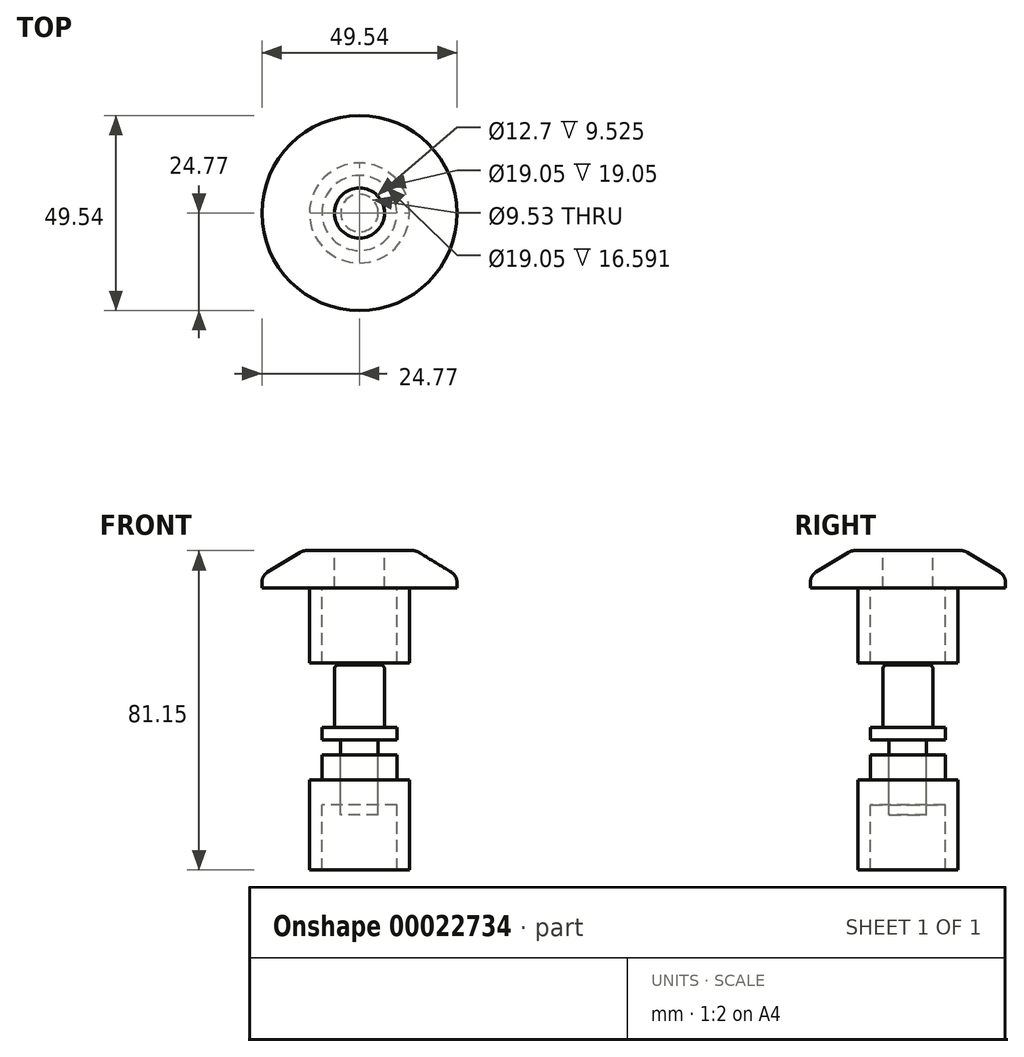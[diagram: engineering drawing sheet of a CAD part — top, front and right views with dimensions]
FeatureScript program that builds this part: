
annotation { "Feature Type Name" : "Feature", "Feature Type Description" : "" }
export const myFeature = defineFeature(function(context is Context, id is Id, definition is map)
    precondition{}
    {
        {
            var Q0;
            Q0=qCreatedBy(makeId("Front.planeOp"),FACE);
            var sketch = newSketch(context, id + "F0", { "sketchPlane" : qUnion([Q0])});
            skLineSegment(sketch, "E0", {"start": v(0, 45.49) * mm, "end": v(0, -47.52) * mm, "construction": true});
            skLineSegment(sketch, "E1", {"start": v(-6.35, 9.53) * mm, "end": v(-14.35, 9.53) * mm});
            skLineSegment(sketch, "E2", {"start": v(-14.35, 9.53) * mm, "end": v(-24.77, 3.17) * mm});
            skLineSegment(sketch, "E3", {"start": v(-24.76, 3.17) * mm, "end": v(-24.76, 0) * mm});
            skLineSegment(sketch, "E4", {"start": v(-24.76, 0) * mm, "end": v(-12.7, 0) * mm});
            skLineSegment(sketch, "E5", {"start": v(-12.7, 0) * mm, "end": v(-12.7, -19.05) * mm});
            skLineSegment(sketch, "E6", {"start": v(-12.7, -19.05) * mm, "end": v(-9.52, -19.05) * mm});
            skLineSegment(sketch, "E7", {"start": v(-9.52, -19.05) * mm, "end": v(-9.52, 0) * mm});
            skLineSegment(sketch, "E8", {"start": v(-9.52, 0) * mm, "end": v(-6.35, 0) * mm});
            skLineSegment(sketch, "E9", {"start": v(-6.35, 0) * mm, "end": v(-6.35, 9.53) * mm});
            skSolve(sketch);
        }
        {
            var Q0;
            Q0 = qSketchRegion(id + "F0", true);
            var Q1;
            Q1=sQuery(id+"F0.wireOp",EDGE,"E0");
            revolve(context, id + "F1", {"entities" : qUnion([Q0]), "axis" : qUnion([Q1]), "revolveType" : RevolveType.FULL});
        }
        {
            var Q0;
            Q0=makeQuery(id+"F1.opRevolve","SWEPT_EDGE",EDGE,{"disambiguationData":[OSD([sQuery(id+"F0.wireOp",EDGE,"E1"),sQuery(id+"F0.wireOp",EDGE,"E2")])]});
            var Q1;
            Q1=makeQuery(id+"F1.opRevolve","SWEPT_EDGE",EDGE,{"disambiguationData":[OSD([sQuery(id+"F0.wireOp",EDGE,"E2"),sQuery(id+"F0.wireOp",EDGE,"E3")])]});
            fillet(context, id + "F2", {"entities" : qUnion([Q0, Q1]), "radius" : 3 * mm, "tangentPropagation" : true, "allowEdgeOverflow" : false});
        }
        {
            var Q0;
            Q0=qCreatedBy(makeId("Front.planeOp"),FACE);
            var sketch = newSketch(context, id + "F3", { "sketchPlane" : qUnion([Q0])});
            skLineSegment(sketch, "E10", {"start": v(0, 93.32) * mm, "end": v(0, -112.82) * mm, "construction": true});
            skLineSegment(sketch, "E11", {"start": v(-4.76, -57.61) * mm, "end": v(-4.76, -38.56) * mm});
            skLineSegment(sketch, "E12", {"start": v(-4.76, -38.56) * mm, "end": v(-9.52, -38.56) * mm});
            skLineSegment(sketch, "E13", {"start": v(-9.52, -38.56) * mm, "end": v(-9.52, -35.39) * mm});
            skLineSegment(sketch, "E14", {"start": v(-9.52, -35.39) * mm, "end": v(-6.35, -35.39) * mm});
            skLineSegment(sketch, "E15", {"start": v(-6.35, -35.39) * mm, "end": v(-6.35, -19.51) * mm});
            skLineSegment(sketch, "E16", {"start": v(-6.35, -19.51) * mm, "end": v(0, -19.51) * mm});
            skLineSegment(sketch, "E17", {"start": v(0, -19.51) * mm, "end": v(0, -57.61) * mm});
            skLineSegment(sketch, "E18", {"start": v(0, -57.61) * mm, "end": v(-4.76, -57.61) * mm});
            skSolve(sketch);
        }
        {
            var Q0;
            Q0 = qSketchRegion(id + "F3", true);
            var Q1;
            Q1=sQuery(id+"F3.wireOp",EDGE,"E10");
            revolve(context, id + "F4", {"entities" : qUnion([Q0]), "axis" : qUnion([Q1]), "revolveType" : RevolveType.FULL});
        }
        {
            var Q0;
            Q0=makeQuery(id+"F4.opRevolve","SWEPT_EDGE",EDGE,{"disambiguationData":[OSD([sQuery(id+"F3.wireOp",EDGE,"E15"),sQuery(id+"F3.wireOp",EDGE,"E16")])]});
            fillet(context, id + "F5", {"entities" : qUnion([Q0]), "radius" : 1 * mm, "tangentPropagation" : true, "allowEdgeOverflow" : false});
        }
        {
            var Q0;
            Q0=qCreatedBy(makeId("Front.planeOp"),FACE);
            var sketch = newSketch(context, id + "F6", { "sketchPlane" : qUnion([Q0])});
            skLineSegment(sketch, "E19", {"start": v(0, 44.63) * mm, "end": v(0, -78.76) * mm, "construction": true});
            skLineSegment(sketch, "E20", {"start": v(4.76, -42.33) * mm, "end": v(4.76, -55.03) * mm});
            skLineSegment(sketch, "E21", {"start": v(4.76, -55.03) * mm, "end": v(9.53, -55.03) * mm});
            skLineSegment(sketch, "E22", {"start": v(9.53, -55.03) * mm, "end": v(9.53, -71.62) * mm});
            skLineSegment(sketch, "E23", {"start": v(9.53, -71.62) * mm, "end": v(12.7, -71.62) * mm});
            skLineSegment(sketch, "E24", {"start": v(12.7, -71.62) * mm, "end": v(12.7, -48.68) * mm});
            skLineSegment(sketch, "E25", {"start": v(12.7, -48.68) * mm, "end": v(9.53, -48.68) * mm});
            skLineSegment(sketch, "E26", {"start": v(9.53, -48.68) * mm, "end": v(9.53, -42.33) * mm});
            skLineSegment(sketch, "E27", {"start": v(9.53, -42.33) * mm, "end": v(4.76, -42.33) * mm});
            skSolve(sketch);
        }
        {
            var Q0;
            Q0 = qSketchRegion(id + "F6", true);
            var Q1;
            Q1=sQuery(id+"F6.wireOp",EDGE,"E19");
            revolve(context, id + "F7", {"entities" : qUnion([Q0]), "axis" : qUnion([Q1]), "revolveType" : RevolveType.FULL});
        }
    });
